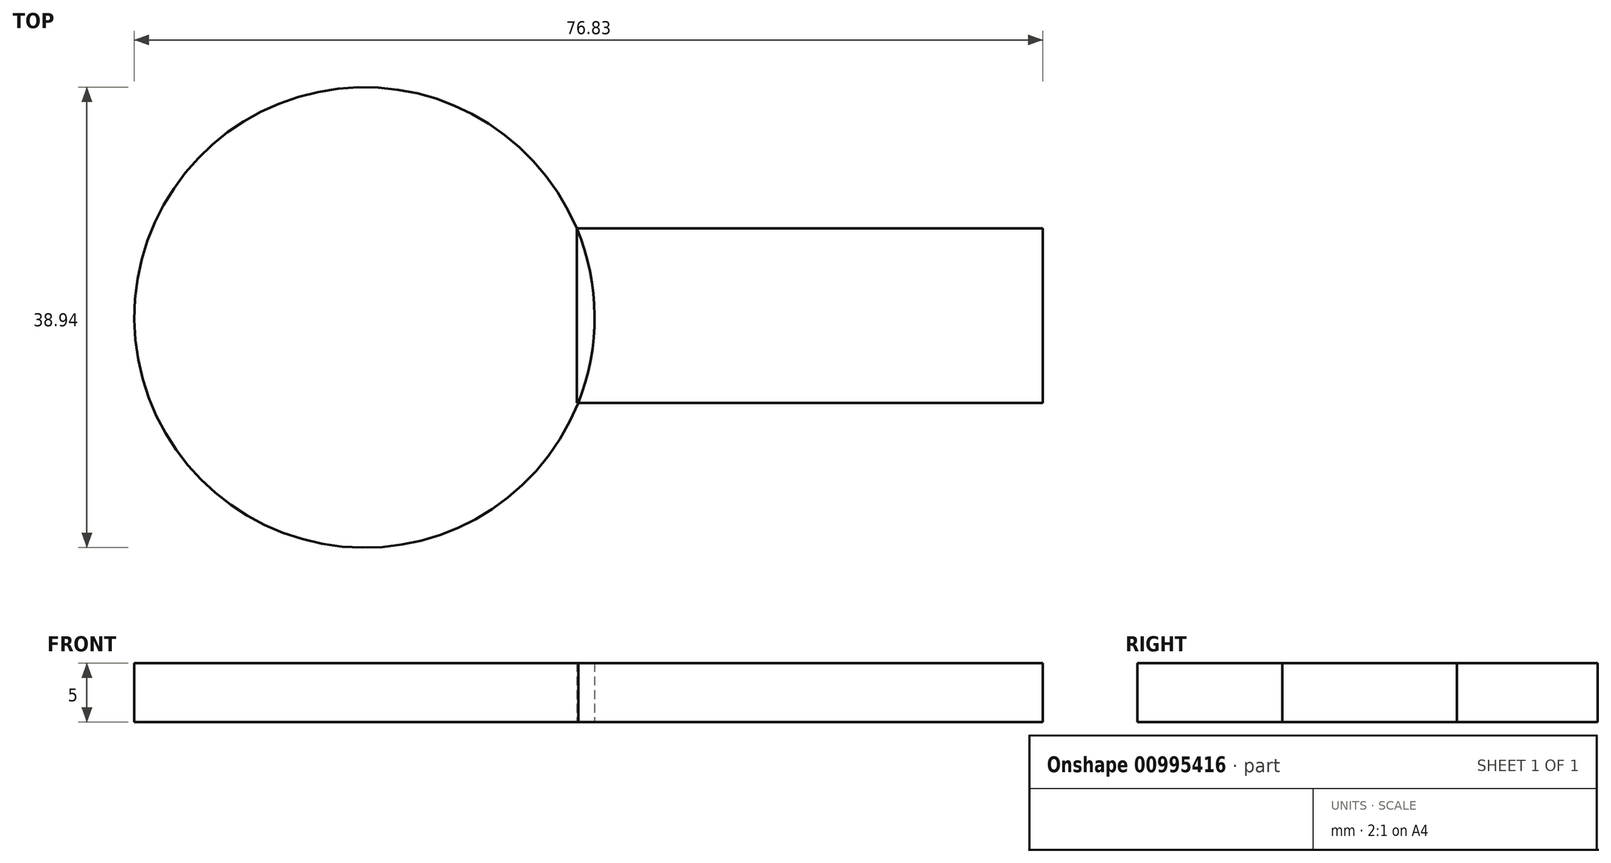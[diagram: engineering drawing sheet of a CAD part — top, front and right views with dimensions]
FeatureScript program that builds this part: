
annotation { "Feature Type Name" : "Feature", "Feature Type Description" : "" }
export const myFeature = defineFeature(function(context is Context, id is Id, definition is map)
    precondition{}
    {
        {
            var Q0;
            Q0=qCreatedBy(makeId("Top.planeOp"),FACE);
            var sketch = newSketch(context, id + "F0", { "sketchPlane" : qUnion([Q0])});
            skCircle(sketch, "E0", {"center": v(0, 0) * mm, "radius": 19.47 * mm});
            skLineSegment(sketch, "E1.bottom", {"start": v(17.95, 7.54) * mm, "end": v(57.36, 7.54) * mm});
            skLineSegment(sketch, "E1.top", {"start": v(17.95, -7.22) * mm, "end": v(57.36, -7.22) * mm});
            skLineSegment(sketch, "E1.left", {"start": v(17.95, 7.54) * mm, "end": v(17.95, -7.22) * mm});
            skLineSegment(sketch, "E1.right", {"start": v(57.36, 7.54) * mm, "end": v(57.36, -7.22) * mm});
            skSolve(sketch);
        }
        {
            var Q0;
            {var subQ0=sQuery(id+"F0.wireOp",EDGE,"E1.left");Q0=makeQuery(id+"F0.imprint","IMPRINT",FACE,{"disambiguationData":[TD([[makeQuery(id+"F0.imprint","IMPRINT",EDGE,{"derivedFrom":subQ0}),-1.0]])]});}
            var Q1;
            {var subQ0=sQuery(id+"F0.wireOp",EDGE,"E1.bottom");Q1=makeQuery(id+"F0.imprint","IMPRINT",FACE,{"disambiguationData":[TD([[makeQuery(id+"F0.imprint","IMPRINT",EDGE,{"derivedFrom":subQ0}),-1.0]])]});}
            extrude(context, id + "F1", {"entities" : qUnion([Q0, Q1]), "depth" : 5 * mm, "offsetDistance" : 25 * mm});
        }
    });
